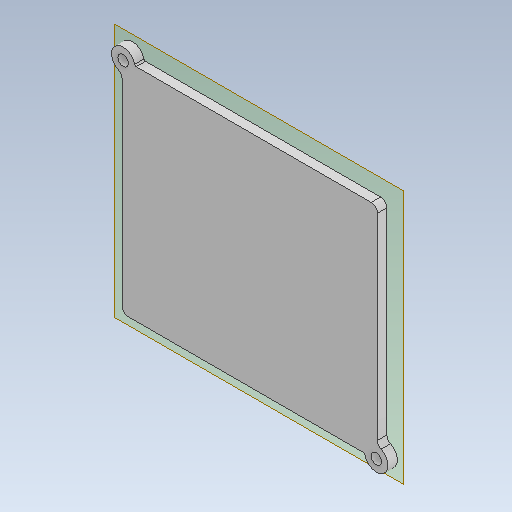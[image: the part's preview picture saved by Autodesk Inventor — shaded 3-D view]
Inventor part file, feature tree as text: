
AUTODESK INVENTOR PART (.ipt)
format: ipt  version: 2021.3 (Build 253353010, 353A)  size: 146,432 bytes
history: native  units: mm
features: reference x28, other x3, extrude x2, sketch x2, plane x1
ambient origin geometry x8: Origin, YZ Plane, XZ Plane, XY Plane, X Axis, Y Axis, Z Axis, Center Point
bodies: Volumenkörper1 (feature_tree)
feature tree (36):
  extrude  "Extrusion1"  TaperAngle=0.0deg  [1 undecoded]
  plane  "Arbeitsebene1"
  extrude  "Extrusion2"  Depth=1.0mm
  sketch  "Skizze1"  dims[d0=3.0mm d1=0.0mm d2=0.0mm]
  reference  "Referenz1"
  reference  "Referenz2"
  reference  "Referenz3"
  reference  "Referenz4"
  reference  "Referenz5"
  reference  "Referenz6"
  reference  "Referenz7"
  reference  "Referenz8"
  reference  "Referenz9"
  reference  "Referenz10"
  reference  "Referenz11"
  reference  "Referenz12"
  reference  "Referenz13"
  reference  "Referenz14"
  reference  "Referenz15"
  reference  "Referenz16"
  sketch  "Skizze2"  dims[d4=1.0mm d5=0.0mm d6=3.4mm d7=0.2mm d8=2.0mm d9=1.0mm]
  reference  "Referenz17"
  reference  "Referenz18"
  reference  "Referenz19"
  reference  "Referenz20"
  reference  "Referenz24"
  reference  "Referenz25"
  reference  "Referenz26"
  reference  "Referenz27"
  reference  "Referenz28"
  reference  "Referenz29"
  reference  "Referenz30"
  reference  "Referenz31"
  other  "<userpath>\Documents\Inventor\MotorController\gehaeuse_bg.iam"
  other  "gehaeuse_bg.iam"
  other  "gehause:1"
note: 1 required parameter value undecoded (feature->parameter linkage not recoverable at this tier; creation-order binding heuristic only, values carry confidence <= 0.55)
